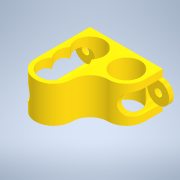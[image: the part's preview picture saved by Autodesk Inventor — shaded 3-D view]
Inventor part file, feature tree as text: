
AUTODESK INVENTOR PART (.ipt)
format: ipt  version: 2020 (Build 240168000, 168)  size: 214,016 bytes
history: native  units: in
note: dims shown in document units (in); Inventor stores cm internally (conversion verified against a paired STEP export)
features: extrude x5, sketch x5, projected_geometry x2, fillet x1
ambient origin geometry x8: Origin, YZ Plane, XZ Plane, XY Plane, X Axis, Y Axis, Z Axis, Center Point
bodies: Solid1 (feature_tree)
feature tree (13):
  extrude  "Extrusion1"  Depth=1.0in
  extrude  "Extrusion2"  Depth=1.0in
  extrude  "Extrusion3"  Depth=0.125in TaperAngle=0.0deg
  extrude  "Extrusion4"  Depth=1.0in TaperAngle=0.0deg
  extrude  "Extrusion5"  Depth=0.5in
  fillet  "Fillet1"  Radius=1.5in
  sketch  "Sketch1"  dims[d0=2.0in d1=1.0in]
  sketch  "Sketch2"  dims[d2=0.5in d3=1.0in]
  projected_geometry  "Projected Loop1"
  sketch  "Sketch4"  dims[d4=0.6in d5=0.125in d6=0.0in]
  projected_geometry  "Projected Loop2"
  sketch  "Sketch5"  dims[d7=0.875in d8=0.0in d9=1.0in d10=0.0in]
  sketch  "Sketch6"  dims[d11=0.7736in d12=0.5in d13=1.5in d14=1.1811in d16=0.5in d17=0.7874in d19=1.0in d22=0.0in d23=0.0in d24=0.203in d25=0.0in d26=0.0in d27=0.5in]
